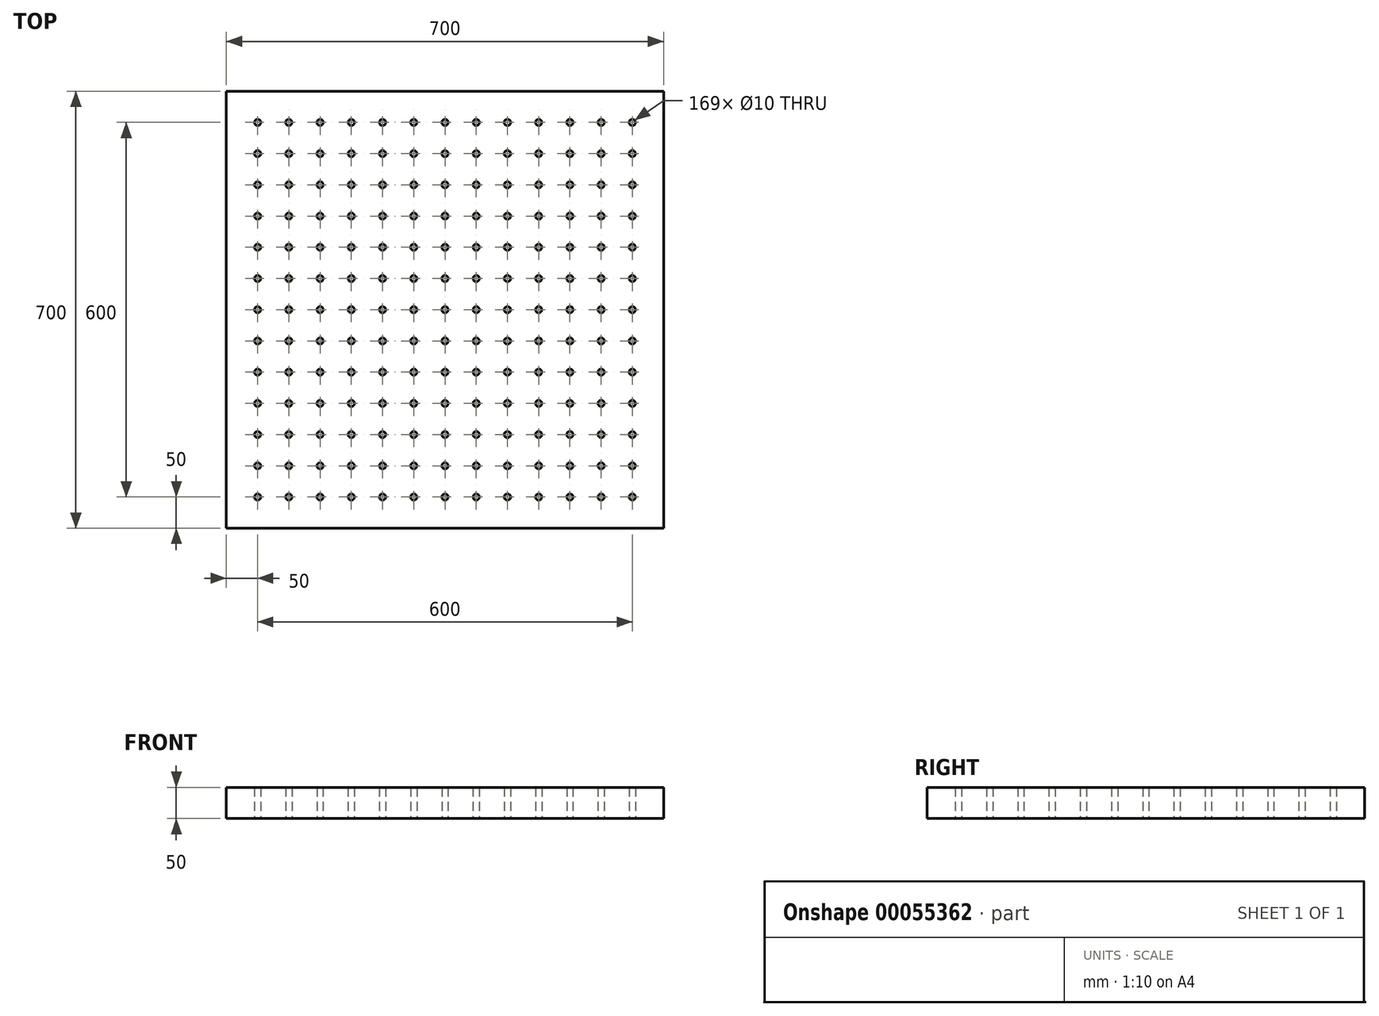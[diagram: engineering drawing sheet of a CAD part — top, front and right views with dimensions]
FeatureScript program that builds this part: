
annotation { "Feature Type Name" : "Feature", "Feature Type Description" : "" }
export const myFeature = defineFeature(function(context is Context, id is Id, definition is map)
    precondition{}
    {
        {
            var Q0;
            Q0=qCreatedBy(makeId("Top.planeOp"),FACE);
            var sketch = newSketch(context, id + "F0", { "sketchPlane" : qUnion([Q0])});
            skCircle(sketch, "E0", {"center": v(-300, -300) * mm, "radius": 5 * mm});
            skCircle(sketch, "E1.0.1.0", {"center": v(-300, -250) * mm, "radius": 5 * mm});
            skCircle(sketch, "E1.0.2.0", {"center": v(-300, -200) * mm, "radius": 5 * mm});
            skCircle(sketch, "E1.0.3.0", {"center": v(-300, -150) * mm, "radius": 5 * mm});
            skCircle(sketch, "E1.0.4.0", {"center": v(-300, -100) * mm, "radius": 5 * mm});
            skCircle(sketch, "E1.0.5.0", {"center": v(-300, -50) * mm, "radius": 5 * mm});
            skCircle(sketch, "E1.0.6.0", {"center": v(-300, 0) * mm, "radius": 5 * mm});
            skCircle(sketch, "E1.0.7.0", {"center": v(-300, 50) * mm, "radius": 5 * mm});
            skCircle(sketch, "E1.0.8.0", {"center": v(-300, 100) * mm, "radius": 5 * mm});
            skCircle(sketch, "E1.0.9.0", {"center": v(-300, 150) * mm, "radius": 5 * mm});
            skCircle(sketch, "E1.1.0.0", {"center": v(-250, -300) * mm, "radius": 5 * mm});
            skCircle(sketch, "E1.1.1.0", {"center": v(-250, -250) * mm, "radius": 5 * mm});
            skCircle(sketch, "E1.1.2.0", {"center": v(-250, -200) * mm, "radius": 5 * mm});
            skCircle(sketch, "E1.1.3.0", {"center": v(-250, -150) * mm, "radius": 5 * mm});
            skCircle(sketch, "E1.1.4.0", {"center": v(-250, -100) * mm, "radius": 5 * mm});
            skCircle(sketch, "E1.1.5.0", {"center": v(-250, -50) * mm, "radius": 5 * mm});
            skCircle(sketch, "E1.1.6.0", {"center": v(-250, 0) * mm, "radius": 5 * mm});
            skCircle(sketch, "E1.1.7.0", {"center": v(-250, 50) * mm, "radius": 5 * mm});
            skCircle(sketch, "E1.1.8.0", {"center": v(-250, 100) * mm, "radius": 5 * mm});
            skCircle(sketch, "E1.1.9.0", {"center": v(-250, 150) * mm, "radius": 5 * mm});
            skCircle(sketch, "E1.2.0.0", {"center": v(-200, -300) * mm, "radius": 5 * mm});
            skCircle(sketch, "E1.2.1.0", {"center": v(-200, -250) * mm, "radius": 5 * mm});
            skCircle(sketch, "E1.2.2.0", {"center": v(-200, -200) * mm, "radius": 5 * mm});
            skCircle(sketch, "E1.2.3.0", {"center": v(-200, -150) * mm, "radius": 5 * mm});
            skCircle(sketch, "E1.2.4.0", {"center": v(-200, -100) * mm, "radius": 5 * mm});
            skCircle(sketch, "E1.2.5.0", {"center": v(-200, -50) * mm, "radius": 5 * mm});
            skCircle(sketch, "E1.2.6.0", {"center": v(-200, 0) * mm, "radius": 5 * mm});
            skCircle(sketch, "E1.2.7.0", {"center": v(-200, 50) * mm, "radius": 5 * mm});
            skCircle(sketch, "E1.2.8.0", {"center": v(-200, 100) * mm, "radius": 5 * mm});
            skCircle(sketch, "E1.2.9.0", {"center": v(-200, 150) * mm, "radius": 5 * mm});
            skCircle(sketch, "E1.3.0.0", {"center": v(-150, -300) * mm, "radius": 5 * mm});
            skCircle(sketch, "E1.3.1.0", {"center": v(-150, -250) * mm, "radius": 5 * mm});
            skCircle(sketch, "E1.3.2.0", {"center": v(-150, -200) * mm, "radius": 5 * mm});
            skCircle(sketch, "E1.3.3.0", {"center": v(-150, -150) * mm, "radius": 5 * mm});
            skCircle(sketch, "E1.3.4.0", {"center": v(-150, -100) * mm, "radius": 5 * mm});
            skCircle(sketch, "E1.3.5.0", {"center": v(-150, -50) * mm, "radius": 5 * mm});
            skCircle(sketch, "E1.3.6.0", {"center": v(-150, 0) * mm, "radius": 5 * mm});
            skCircle(sketch, "E1.3.7.0", {"center": v(-150, 50) * mm, "radius": 5 * mm});
            skCircle(sketch, "E1.3.8.0", {"center": v(-150, 100) * mm, "radius": 5 * mm});
            skCircle(sketch, "E1.3.9.0", {"center": v(-150, 150) * mm, "radius": 5 * mm});
            skCircle(sketch, "E1.4.0.0", {"center": v(-100, -300) * mm, "radius": 5 * mm});
            skCircle(sketch, "E1.4.1.0", {"center": v(-100, -250) * mm, "radius": 5 * mm});
            skCircle(sketch, "E1.4.2.0", {"center": v(-100, -200) * mm, "radius": 5 * mm});
            skCircle(sketch, "E1.4.3.0", {"center": v(-100, -150) * mm, "radius": 5 * mm});
            skCircle(sketch, "E1.4.4.0", {"center": v(-100, -100) * mm, "radius": 5 * mm});
            skCircle(sketch, "E1.4.5.0", {"center": v(-100, -50) * mm, "radius": 5 * mm});
            skCircle(sketch, "E1.4.6.0", {"center": v(-100, 0) * mm, "radius": 5 * mm});
            skCircle(sketch, "E1.4.7.0", {"center": v(-100, 50) * mm, "radius": 5 * mm});
            skCircle(sketch, "E1.4.8.0", {"center": v(-100, 100) * mm, "radius": 5 * mm});
            skCircle(sketch, "E1.4.9.0", {"center": v(-100, 150) * mm, "radius": 5 * mm});
            skCircle(sketch, "E1.5.0.0", {"center": v(-50, -300) * mm, "radius": 5 * mm});
            skCircle(sketch, "E1.5.1.0", {"center": v(-50, -250) * mm, "radius": 5 * mm});
            skCircle(sketch, "E1.5.2.0", {"center": v(-50, -200) * mm, "radius": 5 * mm});
            skCircle(sketch, "E1.5.3.0", {"center": v(-50, -150) * mm, "radius": 5 * mm});
            skCircle(sketch, "E1.5.4.0", {"center": v(-50, -100) * mm, "radius": 5 * mm});
            skCircle(sketch, "E1.5.5.0", {"center": v(-50, -50) * mm, "radius": 5 * mm});
            skCircle(sketch, "E1.5.6.0", {"center": v(-50, 0) * mm, "radius": 5 * mm});
            skCircle(sketch, "E1.5.7.0", {"center": v(-50, 50) * mm, "radius": 5 * mm});
            skCircle(sketch, "E1.5.8.0", {"center": v(-50, 100) * mm, "radius": 5 * mm});
            skCircle(sketch, "E1.5.9.0", {"center": v(-50, 150) * mm, "radius": 5 * mm});
            skCircle(sketch, "E1.6.0.0", {"center": v(0, -300) * mm, "radius": 5 * mm});
            skCircle(sketch, "E1.6.1.0", {"center": v(0, -250) * mm, "radius": 5 * mm});
            skCircle(sketch, "E1.6.2.0", {"center": v(0, -200) * mm, "radius": 5 * mm});
            skCircle(sketch, "E1.6.3.0", {"center": v(0, -150) * mm, "radius": 5 * mm});
            skCircle(sketch, "E1.6.4.0", {"center": v(0, -100) * mm, "radius": 5 * mm});
            skCircle(sketch, "E1.6.5.0", {"center": v(0, -50) * mm, "radius": 5 * mm});
            skCircle(sketch, "E1.6.6.0", {"center": v(0, 0) * mm, "radius": 5 * mm});
            skCircle(sketch, "E1.6.7.0", {"center": v(0, 50) * mm, "radius": 5 * mm});
            skCircle(sketch, "E1.6.8.0", {"center": v(0, 100) * mm, "radius": 5 * mm});
            skCircle(sketch, "E1.6.9.0", {"center": v(0, 150) * mm, "radius": 5 * mm});
            skCircle(sketch, "E1.7.0.0", {"center": v(50, -300) * mm, "radius": 5 * mm});
            skCircle(sketch, "E1.7.1.0", {"center": v(50, -250) * mm, "radius": 5 * mm});
            skCircle(sketch, "E1.7.2.0", {"center": v(50, -200) * mm, "radius": 5 * mm});
            skCircle(sketch, "E1.7.3.0", {"center": v(50, -150) * mm, "radius": 5 * mm});
            skCircle(sketch, "E1.7.4.0", {"center": v(50, -100) * mm, "radius": 5 * mm});
            skCircle(sketch, "E1.7.5.0", {"center": v(50, -50) * mm, "radius": 5 * mm});
            skCircle(sketch, "E1.7.6.0", {"center": v(50, 0) * mm, "radius": 5 * mm});
            skCircle(sketch, "E1.7.7.0", {"center": v(50, 50) * mm, "radius": 5 * mm});
            skCircle(sketch, "E1.7.8.0", {"center": v(50, 100) * mm, "radius": 5 * mm});
            skCircle(sketch, "E1.7.9.0", {"center": v(50, 150) * mm, "radius": 5 * mm});
            skCircle(sketch, "E1.8.0.0", {"center": v(100, -300) * mm, "radius": 5 * mm});
            skCircle(sketch, "E1.8.1.0", {"center": v(100, -250) * mm, "radius": 5 * mm});
            skCircle(sketch, "E1.8.2.0", {"center": v(100, -200) * mm, "radius": 5 * mm});
            skCircle(sketch, "E1.8.3.0", {"center": v(100, -150) * mm, "radius": 5 * mm});
            skCircle(sketch, "E1.8.4.0", {"center": v(100, -100) * mm, "radius": 5 * mm});
            skCircle(sketch, "E1.8.5.0", {"center": v(100, -50) * mm, "radius": 5 * mm});
            skCircle(sketch, "E1.8.6.0", {"center": v(100, 0) * mm, "radius": 5 * mm});
            skCircle(sketch, "E1.8.7.0", {"center": v(100, 50) * mm, "radius": 5 * mm});
            skCircle(sketch, "E1.8.8.0", {"center": v(100, 100) * mm, "radius": 5 * mm});
            skCircle(sketch, "E1.8.9.0", {"center": v(100, 150) * mm, "radius": 5 * mm});
            skCircle(sketch, "E1.9.0.0", {"center": v(150, -300) * mm, "radius": 5 * mm});
            skCircle(sketch, "E1.9.1.0", {"center": v(150, -250) * mm, "radius": 5 * mm});
            skCircle(sketch, "E1.9.2.0", {"center": v(150, -200) * mm, "radius": 5 * mm});
            skCircle(sketch, "E1.9.3.0", {"center": v(150, -150) * mm, "radius": 5 * mm});
            skCircle(sketch, "E1.9.4.0", {"center": v(150, -100) * mm, "radius": 5 * mm});
            skCircle(sketch, "E1.9.5.0", {"center": v(150, -50) * mm, "radius": 5 * mm});
            skCircle(sketch, "E1.9.6.0", {"center": v(150, 0) * mm, "radius": 5 * mm});
            skCircle(sketch, "E1.9.7.0", {"center": v(150, 50) * mm, "radius": 5 * mm});
            skCircle(sketch, "E1.9.8.0", {"center": v(150, 100) * mm, "radius": 5 * mm});
            skCircle(sketch, "E1.9.9.0", {"center": v(150, 150) * mm, "radius": 5 * mm});
            skLineSegment(sketch, "E1.direction1", {"start": v(-300, -300) * mm, "end": v(-250, -300) * mm, "construction": true});
            skLineSegment(sketch, "E1.direction2", {"start": v(-300, -300) * mm, "end": v(-300, -250) * mm, "construction": true});
            skCircle(sketch, "E2.0.10.0", {"center": v(200, -300) * mm, "radius": 5 * mm});
            skCircle(sketch, "E2.0.10.1", {"center": v(200, -250) * mm, "radius": 5 * mm});
            skCircle(sketch, "E2.0.10.2", {"center": v(200, -200) * mm, "radius": 5 * mm});
            skCircle(sketch, "E2.0.10.3", {"center": v(200, -150) * mm, "radius": 5 * mm});
            skCircle(sketch, "E2.0.10.4", {"center": v(200, -100) * mm, "radius": 5 * mm});
            skCircle(sketch, "E2.0.10.5", {"center": v(200, -50) * mm, "radius": 5 * mm});
            skCircle(sketch, "E2.0.10.6", {"center": v(200, 0) * mm, "radius": 5 * mm});
            skCircle(sketch, "E2.0.10.7", {"center": v(200, 50) * mm, "radius": 5 * mm});
            skCircle(sketch, "E2.0.10.8", {"center": v(200, 100) * mm, "radius": 5 * mm});
            skCircle(sketch, "E2.0.10.9", {"center": v(200, 150) * mm, "radius": 5 * mm});
            skCircle(sketch, "E2.0.11.0", {"center": v(250, -300) * mm, "radius": 5 * mm});
            skCircle(sketch, "E2.0.11.1", {"center": v(250, -250) * mm, "radius": 5 * mm});
            skCircle(sketch, "E2.0.11.2", {"center": v(250, -200) * mm, "radius": 5 * mm});
            skCircle(sketch, "E2.0.11.3", {"center": v(250, -150) * mm, "radius": 5 * mm});
            skCircle(sketch, "E2.0.11.4", {"center": v(250, -100) * mm, "radius": 5 * mm});
            skCircle(sketch, "E2.0.11.5", {"center": v(250, -50) * mm, "radius": 5 * mm});
            skCircle(sketch, "E2.0.11.6", {"center": v(250, 0) * mm, "radius": 5 * mm});
            skCircle(sketch, "E2.0.11.7", {"center": v(250, 50) * mm, "radius": 5 * mm});
            skCircle(sketch, "E2.0.11.8", {"center": v(250, 100) * mm, "radius": 5 * mm});
            skCircle(sketch, "E2.0.11.9", {"center": v(250, 150) * mm, "radius": 5 * mm});
            skCircle(sketch, "E2.0.12.0", {"center": v(300, -300) * mm, "radius": 5 * mm});
            skCircle(sketch, "E2.0.12.1", {"center": v(300, -250) * mm, "radius": 5 * mm});
            skCircle(sketch, "E2.0.12.2", {"center": v(300, -200) * mm, "radius": 5 * mm});
            skCircle(sketch, "E2.0.12.3", {"center": v(300, -150) * mm, "radius": 5 * mm});
            skCircle(sketch, "E2.0.12.4", {"center": v(300, -100) * mm, "radius": 5 * mm});
            skCircle(sketch, "E2.0.12.5", {"center": v(300, -50) * mm, "radius": 5 * mm});
            skCircle(sketch, "E2.0.12.6", {"center": v(300, 0) * mm, "radius": 5 * mm});
            skCircle(sketch, "E2.0.12.7", {"center": v(300, 50) * mm, "radius": 5 * mm});
            skCircle(sketch, "E2.0.12.8", {"center": v(300, 100) * mm, "radius": 5 * mm});
            skCircle(sketch, "E2.0.12.9", {"center": v(300, 150) * mm, "radius": 5 * mm});
            skCircle(sketch, "E3.0.0.10", {"center": v(-300, 200) * mm, "radius": 5 * mm});
            skCircle(sketch, "E3.0.0.11", {"center": v(-300, 250) * mm, "radius": 5 * mm});
            skCircle(sketch, "E3.0.0.12", {"center": v(-300, 300) * mm, "radius": 5 * mm});
            skCircle(sketch, "E3.0.1.10", {"center": v(-250, 200) * mm, "radius": 5 * mm});
            skCircle(sketch, "E3.0.1.11", {"center": v(-250, 250) * mm, "radius": 5 * mm});
            skCircle(sketch, "E3.0.1.12", {"center": v(-250, 300) * mm, "radius": 5 * mm});
            skCircle(sketch, "E3.0.2.10", {"center": v(-200, 200) * mm, "radius": 5 * mm});
            skCircle(sketch, "E3.0.2.11", {"center": v(-200, 250) * mm, "radius": 5 * mm});
            skCircle(sketch, "E3.0.2.12", {"center": v(-200, 300) * mm, "radius": 5 * mm});
            skCircle(sketch, "E3.0.3.10", {"center": v(-150, 200) * mm, "radius": 5 * mm});
            skCircle(sketch, "E3.0.3.11", {"center": v(-150, 250) * mm, "radius": 5 * mm});
            skCircle(sketch, "E3.0.3.12", {"center": v(-150, 300) * mm, "radius": 5 * mm});
            skCircle(sketch, "E3.0.4.10", {"center": v(-100, 200) * mm, "radius": 5 * mm});
            skCircle(sketch, "E3.0.4.11", {"center": v(-100, 250) * mm, "radius": 5 * mm});
            skCircle(sketch, "E3.0.4.12", {"center": v(-100, 300) * mm, "radius": 5 * mm});
            skCircle(sketch, "E3.0.5.10", {"center": v(-50, 200) * mm, "radius": 5 * mm});
            skCircle(sketch, "E3.0.5.11", {"center": v(-50, 250) * mm, "radius": 5 * mm});
            skCircle(sketch, "E3.0.5.12", {"center": v(-50, 300) * mm, "radius": 5 * mm});
            skCircle(sketch, "E3.0.6.10", {"center": v(0, 200) * mm, "radius": 5 * mm});
            skCircle(sketch, "E3.0.6.11", {"center": v(0, 250) * mm, "radius": 5 * mm});
            skCircle(sketch, "E3.0.6.12", {"center": v(0, 300) * mm, "radius": 5 * mm});
            skCircle(sketch, "E3.0.7.10", {"center": v(50, 200) * mm, "radius": 5 * mm});
            skCircle(sketch, "E3.0.7.11", {"center": v(50, 250) * mm, "radius": 5 * mm});
            skCircle(sketch, "E3.0.7.12", {"center": v(50, 300) * mm, "radius": 5 * mm});
            skCircle(sketch, "E3.0.8.10", {"center": v(100, 200) * mm, "radius": 5 * mm});
            skCircle(sketch, "E3.0.8.11", {"center": v(100, 250) * mm, "radius": 5 * mm});
            skCircle(sketch, "E3.0.8.12", {"center": v(100, 300) * mm, "radius": 5 * mm});
            skCircle(sketch, "E3.0.9.10", {"center": v(150, 200) * mm, "radius": 5 * mm});
            skCircle(sketch, "E3.0.9.11", {"center": v(150, 250) * mm, "radius": 5 * mm});
            skCircle(sketch, "E3.0.9.12", {"center": v(150, 300) * mm, "radius": 5 * mm});
            skCircle(sketch, "E3.0.10.10", {"center": v(200, 200) * mm, "radius": 5 * mm});
            skCircle(sketch, "E3.0.10.11", {"center": v(200, 250) * mm, "radius": 5 * mm});
            skCircle(sketch, "E3.0.10.12", {"center": v(200, 300) * mm, "radius": 5 * mm});
            skCircle(sketch, "E3.0.11.10", {"center": v(250, 200) * mm, "radius": 5 * mm});
            skCircle(sketch, "E3.0.11.11", {"center": v(250, 250) * mm, "radius": 5 * mm});
            skCircle(sketch, "E3.0.11.12", {"center": v(250, 300) * mm, "radius": 5 * mm});
            skCircle(sketch, "E3.0.12.10", {"center": v(300, 200) * mm, "radius": 5 * mm});
            skCircle(sketch, "E3.0.12.11", {"center": v(300, 250) * mm, "radius": 5 * mm});
            skCircle(sketch, "E3.0.12.12", {"center": v(300, 300) * mm, "radius": 5 * mm});
            skLineSegment(sketch, "E4.rect.bottom", {"start": v(350, 350) * mm, "end": v(-350, 350) * mm});
            skLineSegment(sketch, "E4.rect.top", {"start": v(350, -350) * mm, "end": v(-350, -350) * mm});
            skLineSegment(sketch, "E4.rect.left", {"start": v(350, 350) * mm, "end": v(350, -350) * mm});
            skLineSegment(sketch, "E4.rect.right", {"start": v(-350, 350) * mm, "end": v(-350, -350) * mm});
            skSolve(sketch);
        }
        {
            var Q0;
            Q0=makeQuery(id+"F0.imprint","IMPRINT",FACE,{"disambiguationData":[TD([[makeQuery(id+"F0.imprint","IMPRINT",EDGE,{"derivedFrom":sQuery(id+"F0.wireOp",EDGE,"E0")}),-1.0]])]});
            extrude(context, id + "F1", {"entities" : qUnion([Q0]), "depth" : 50 * mm});
        }
    });
